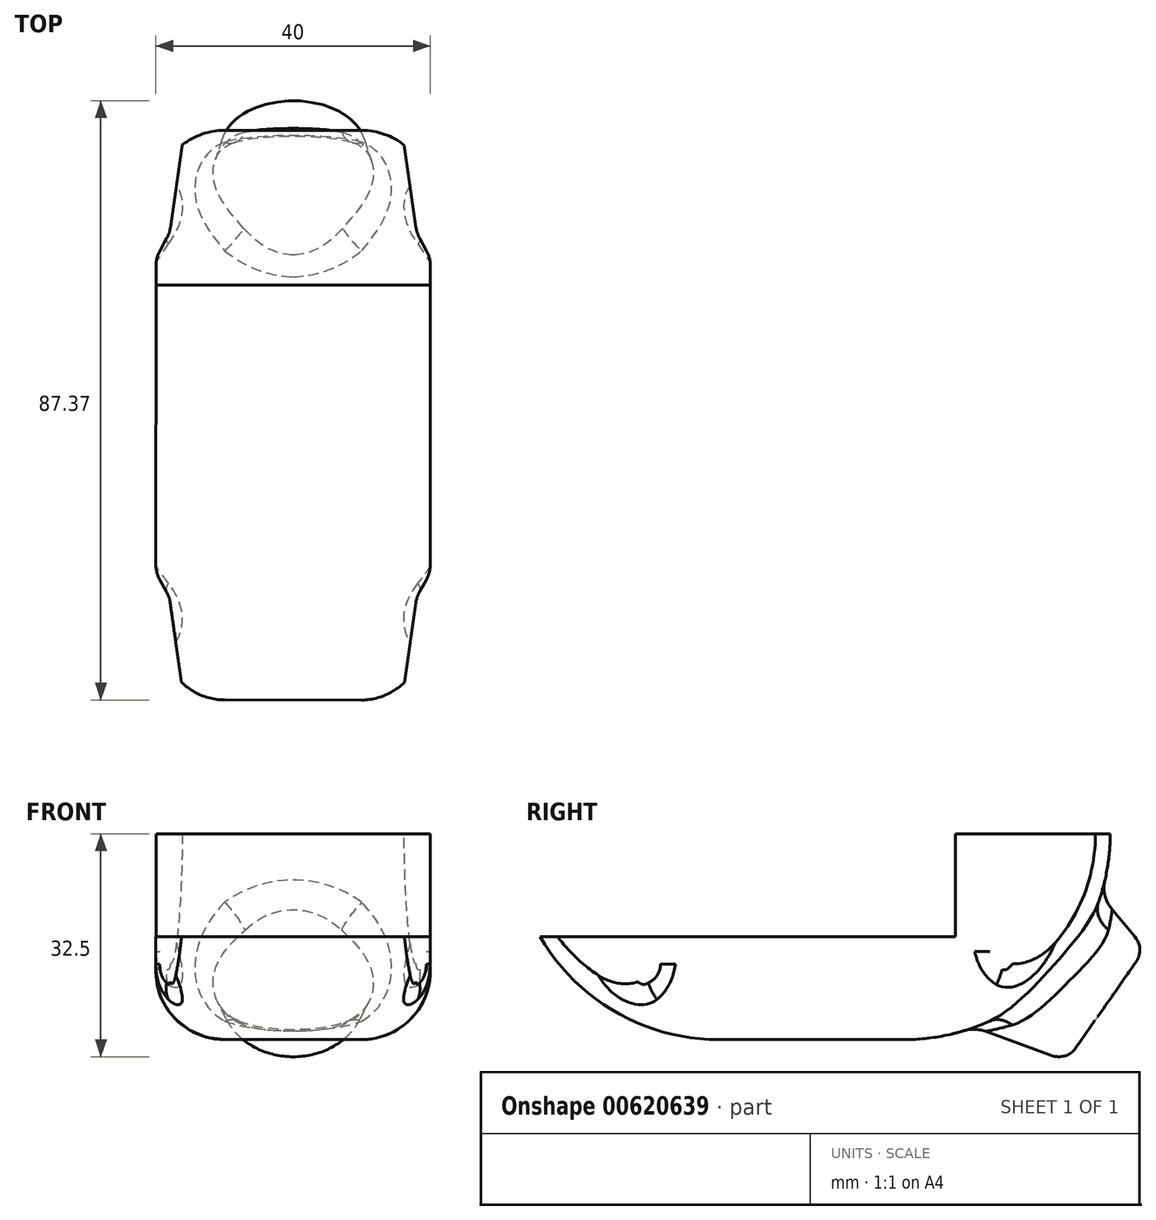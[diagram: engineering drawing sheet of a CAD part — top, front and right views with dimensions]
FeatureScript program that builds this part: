
annotation { "Feature Type Name" : "Feature", "Feature Type Description" : "" }
export const myFeature = defineFeature(function(context is Context, id is Id, definition is map)
    precondition{}
    {
        {
            var Q0;
            Q0=qCreatedBy(makeId("Top.planeOp"),FACE);
            var sketch = newSketch(context, id + "F0", { "sketchPlane" : qUnion([Q0])});
            skLineSegment(sketch, "E0", {"start": v(-20, -22.95) * mm, "end": v(-18.03, -26.5) * mm});
            skLineSegment(sketch, "E1", {"start": v(-18.03, -26.5) * mm, "end": v(-15.88, -41.51) * mm});
            skPoint(sketch, "E2.endSnap0", {"position": v(-0.02, -41.52) * mm});
            skLineSegment(sketch, "E3", {"start": v(-0.02, -41.52) * mm, "end": v(0, 0) * mm, "construction": true});
            skLineSegment(sketch, "E4", {"start": v(-15.88, -41.51) * mm, "end": v(-0.02, -41.52) * mm});
            skLineSegment(sketch, "E5", {"start": v(0, 0) * mm, "end": v(-20, 0.01) * mm, "construction": true});
            skLineSegment(sketch, "E6.MirrorCS", {"start": v(19.98, -22.98) * mm, "end": v(18, -26.52) * mm});
            skLineSegment(sketch, "E7.MirrorCS", {"start": v(18, -26.52) * mm, "end": v(15.84, -41.53) * mm});
            skLineSegment(sketch, "E8.MirrorCS", {"start": v(15.84, -41.53) * mm, "end": v(-0.02, -41.52) * mm});
            skLineSegment(sketch, "E9.MirrorCS", {"start": v(0, 0) * mm, "end": v(20, -0.01) * mm, "construction": true});
            skLineSegment(sketch, "E10", {"start": v(-20, 0.01) * mm, "end": v(-20, -17.03) * mm});
            skLineSegment(sketch, "E11.MirrorCS", {"start": v(20, -0.01) * mm, "end": v(20, -17.05) * mm});
            skLineSegment(sketch, "E12.MirrorCS", {"start": v(18.03, 26.5) * mm, "end": v(15.88, 41.51) * mm});
            skLineSegment(sketch, "E13.MirrorCS", {"start": v(0.02, 41.52) * mm, "end": v(0, 0) * mm, "construction": true});
            skLineSegment(sketch, "E14.MirrorCS", {"start": v(-19.98, 22.98) * mm, "end": v(-18, 26.52) * mm});
            skLineSegment(sketch, "E15.MirrorCS", {"start": v(20, -0.01) * mm, "end": v(20, 17.03) * mm});
            skPoint(sketch, "E16.MirrorP", {"position": v(0.02, 41.52) * mm});
            skLineSegment(sketch, "E17.MirrorCS", {"start": v(-15.84, 41.53) * mm, "end": v(0.02, 41.52) * mm});
            skLineSegment(sketch, "E18.MirrorCS", {"start": v(-18, 26.52) * mm, "end": v(-15.84, 41.53) * mm});
            skLineSegment(sketch, "E19.MirrorCS", {"start": v(-20, 0.01) * mm, "end": v(-20, 17.05) * mm});
            skLineSegment(sketch, "E20.MirrorCS", {"start": v(20, 22.95) * mm, "end": v(18.03, 26.5) * mm});
            skLineSegment(sketch, "E21.MirrorCS", {"start": v(15.88, 41.51) * mm, "end": v(0.02, 41.52) * mm});
            skLineSegment(sketch, "E22", {"start": v(-19.98, 22.98) * mm, "end": v(-20, -22.95) * mm});
            skLineSegment(sketch, "E23", {"start": v(20, 22.95) * mm, "end": v(19.98, -22.98) * mm});
            skSolve(sketch);
        }
        {
            var Q0;
            Q0=makeQuery(id+"F0.imprint","IMPRINT",FACE,{"disambiguationData":[TD([[makeQuery(id+"F0.imprint","IMPRINT",EDGE,{"derivedFrom":sQuery(id+"F0.wireOp",EDGE,"679dddb6-a4d8-4c66-b0c0-365245d2131c.left")}),1.0]])]});
            var Q1;
            Q1=makeQuery(id+"F0.imprint","IMPRINT",FACE,{"disambiguationData":[TD([[makeQuery(id+"F0.imprint","IMPRINT",EDGE,{"derivedFrom":sQuery(id+"F0.wireOp",EDGE,"86fe544a-d19c-4b15-a90d-d04381c5e18d")}),1.0]])]});
            var Q2;
            Q2=makeQuery(id+"F0.imprint","IMPRINT",FACE,{"disambiguationData":[TD([[makeQuery(id+"F0.imprint","IMPRINT",EDGE,{"derivedFrom":sQuery(id+"F0.wireOp",EDGE,"9e7926ad-3512-4c74-b95f-ea411cc99ddc")}),1.0]])]});
            var Q3;
            Q3=makeQuery(id+"F0.imprint","IMPRINT",FACE,{"disambiguationData":[TD([[makeQuery(id+"F0.imprint","IMPRINT",EDGE,{"derivedFrom":sQuery(id+"F0.wireOp",EDGE,"E0")}),1.0]])]});
            extrude(context, id + "F1", {"entities" : qUnion([Q0, Q1, Q2, Q3]), "depth" : 10 * mm, "offsetDistance" : 25 * mm, "hasSecondDirection" : true, "secondDirectionOppositeDirection" : true, "secondDirectionDepth" : 5 * mm});
        }
        {
            var Q0;
            Q0=qCreatedBy(makeId("Top.planeOp"),FACE);
            var sketch = newSketch(context, id + "F2", { "sketchPlane" : qUnion([Q0])});
            skLineSegment(sketch, "E24.MirrorCS", {"start": v(18.03, 26.5) * mm, "end": v(15.88, 41.51) * mm});
            skLineSegment(sketch, "E25.MirrorCS", {"start": v(-19.98, 22.98) * mm, "end": v(-18, 26.52) * mm});
            skPoint(sketch, "E26.MirrorP", {"position": v(0.02, 41.52) * mm});
            skLineSegment(sketch, "E27.MirrorCS", {"start": v(-15.84, 41.53) * mm, "end": v(0.02, 41.52) * mm});
            skLineSegment(sketch, "E28.MirrorCS", {"start": v(-18, 26.52) * mm, "end": v(-15.84, 41.53) * mm});
            skLineSegment(sketch, "E29.MirrorCS", {"start": v(20, 22.95) * mm, "end": v(18.03, 26.5) * mm});
            skLineSegment(sketch, "E30.MirrorCS", {"start": v(15.88, 41.51) * mm, "end": v(0.02, 41.52) * mm});
            skLineSegment(sketch, "E31", {"start": v(-19.98, 19) * mm, "end": v(20, 18.97) * mm});
            skLineSegment(sketch, "E32", {"start": v(-19.98, 22.98) * mm, "end": v(-19.98, 19) * mm});
            skLineSegment(sketch, "E33", {"start": v(20, 22.95) * mm, "end": v(20, 18.97) * mm});
            skSolve(sketch);
        }
        {
            var Q0;
            Q0 = qSketchRegion(id + "F2", true);
            extrude(context, id + "F3", {"entities" : qUnion([Q0]), "operationType" : NewBodyOperationType.ADD, "depth" : 25 * mm, "offsetDistance" : 25 * mm});
        }
        {
            var Q0;
            Q0=makeQuery(id+"F1.opExtrude","CAP_EDGE",EDGE,{"disambiguationData":[OSD([sQuery(id+"F0.wireOp",EDGE,"E17.MirrorCS"),sQuery(id+"F0.wireOp",EDGE,"E21.MirrorCS")])],"isStart":true});
            var Q1;
            Q1=makeQuery(id+"F1.opExtrude","CAP_EDGE",EDGE,{"disambiguationData":[OSD([sQuery(id+"F0.wireOp",EDGE,"E4"),sQuery(id+"F0.wireOp",EDGE,"E8.MirrorCS")])],"isStart":true});
            fillet(context, id + "F4", {"entities" : qUnion([Q0, Q1]), "radius" : 30 * mm, "tangentPropagation" : true, "allowEdgeOverflow" : false});
        }
        {
            var Q0;
            Q0=makeQuery(id+"F1.opExtrude","CAP_EDGE",EDGE,{"disambiguationData":[OSD([sQuery(id+"F0.wireOp",EDGE,"E22")])],"isStart":true});
            var Q1;
            Q1=makeQuery(id+"F1.opExtrude","CAP_EDGE",EDGE,{"disambiguationData":[OSD([sQuery(id+"F0.wireOp",EDGE,"E23")])],"isStart":true});
            fillet(context, id + "F5", {"entities" : qUnion([Q0, Q1]), "radius" : 10 * mm, "tangentPropagation" : true, "allowEdgeOverflow" : false});
        }
        {
            var Q0;
            Q0=makeQuery(id+"F3.boolean.opBoolean","MERGE",EDGE,{"derivedFrom":[makeQuery(id+"F1.opExtrude","SWEPT_EDGE",EDGE,{"disambiguationData":[OSD([sQuery(id+"F0.wireOp",EDGE,"E14.MirrorCS"),sQuery(id+"F0.wireOp",EDGE,"E22")])]}),makeQuery(id+"F3.opExtrude","SWEPT_EDGE",EDGE,{"disambiguationData":[OSD([sQuery(id+"F2.wireOp",EDGE,"E25.MirrorCS"),sQuery(id+"F2.wireOp",EDGE,"E32")])]})]});
            var Q1;
            Q1=makeQuery(id+"F3.boolean.opBoolean","MERGE",EDGE,{"derivedFrom":[makeQuery(id+"F1.opExtrude","SWEPT_EDGE",EDGE,{"disambiguationData":[OSD([sQuery(id+"F0.wireOp",EDGE,"E20.MirrorCS"),sQuery(id+"F0.wireOp",EDGE,"E23")])]}),makeQuery(id+"F3.opExtrude","SWEPT_EDGE",EDGE,{"disambiguationData":[OSD([sQuery(id+"F2.wireOp",EDGE,"E29.MirrorCS"),sQuery(id+"F2.wireOp",EDGE,"E33")])]})]});
            var Q2;
            Q2=makeQuery(id+"F3.boolean.opBoolean","MERGE",EDGE,{"derivedFrom":[makeQuery(id+"F1.opExtrude","SWEPT_EDGE",EDGE,{"disambiguationData":[OSD([sQuery(id+"F0.wireOp",EDGE,"E12.MirrorCS"),sQuery(id+"F0.wireOp",EDGE,"E20.MirrorCS")])]}),makeQuery(id+"F3.opExtrude","SWEPT_EDGE",EDGE,{"disambiguationData":[OSD([sQuery(id+"F2.wireOp",EDGE,"E24.MirrorCS"),sQuery(id+"F2.wireOp",EDGE,"E29.MirrorCS")])]})]});
            var Q3;
            Q3=makeQuery(id+"F3.boolean.opBoolean","MERGE",EDGE,{"derivedFrom":[makeQuery(id+"F1.opExtrude","SWEPT_EDGE",EDGE,{"disambiguationData":[OSD([sQuery(id+"F0.wireOp",EDGE,"E14.MirrorCS"),sQuery(id+"F0.wireOp",EDGE,"E18.MirrorCS")])]}),makeQuery(id+"F3.opExtrude","SWEPT_EDGE",EDGE,{"disambiguationData":[OSD([sQuery(id+"F2.wireOp",EDGE,"E25.MirrorCS"),sQuery(id+"F2.wireOp",EDGE,"E28.MirrorCS")])]})]});
            var Q4;
            Q4=makeQuery(id+"F1.opExtrude","SWEPT_EDGE",EDGE,{"disambiguationData":[OSD([sQuery(id+"F0.wireOp",EDGE,"E0"),sQuery(id+"F0.wireOp",EDGE,"E1")])]});
            var Q5;
            Q5=makeQuery(id+"F1.opExtrude","SWEPT_EDGE",EDGE,{"disambiguationData":[OSD([sQuery(id+"F0.wireOp",EDGE,"E6.MirrorCS"),sQuery(id+"F0.wireOp",EDGE,"E7.MirrorCS")])]});
            var Q6;
            Q6=makeQuery(id+"F1.opExtrude","SWEPT_EDGE",EDGE,{"disambiguationData":[OSD([sQuery(id+"F0.wireOp",EDGE,"E6.MirrorCS"),sQuery(id+"F0.wireOp",EDGE,"E23")])]});
            var Q7;
            Q7=makeQuery(id+"F1.opExtrude","SWEPT_EDGE",EDGE,{"disambiguationData":[OSD([sQuery(id+"F0.wireOp",EDGE,"E0"),sQuery(id+"F0.wireOp",EDGE,"E22")])]});
            fillet(context, id + "F6", {"entities" : qUnion([Q0, Q1, Q2, Q3, Q4, Q5, Q6, Q7]), "radius" : 4.5 * mm, "tangentPropagation" : true, "allowEdgeOverflow" : false});
        }
        {
            var Q0;
            Q0=makeQuery(id+"F4.opFillet","BLEND_EDGE",EDGE,{"blendedFrom":[makeQuery(id+"F1.opExtrude","CAP_EDGE",EDGE,{"disambiguationData":[OSD([sQuery(id+"F0.wireOp",EDGE,"E17.MirrorCS"),sQuery(id+"F0.wireOp",EDGE,"E21.MirrorCS")])],"isStart":true}),makeQuery(id+"F3.opExtrude","CAP_FACE",FACE,{"disambiguationData":[OSD([sQuery(id+"F2.wireOp",EDGE,"E24.MirrorCS"),sQuery(id+"F2.wireOp",EDGE,"E25.MirrorCS"),sQuery(id+"F2.wireOp",EDGE,"E27.MirrorCS"),sQuery(id+"F2.wireOp",EDGE,"E28.MirrorCS"),sQuery(id+"F2.wireOp",EDGE,"E29.MirrorCS"),sQuery(id+"F2.wireOp",EDGE,"E30.MirrorCS"),sQuery(id+"F2.wireOp",EDGE,"E31"),sQuery(id+"F2.wireOp",EDGE,"E32"),sQuery(id+"F2.wireOp",EDGE,"E33")])],"isStart":false})],"blendedInto":[makeQuery(id+"F3.opExtrude","CAP_FACE",FACE,{"disambiguationData":[OSD([sQuery(id+"F2.wireOp",EDGE,"E24.MirrorCS"),sQuery(id+"F2.wireOp",EDGE,"E25.MirrorCS"),sQuery(id+"F2.wireOp",EDGE,"E27.MirrorCS"),sQuery(id+"F2.wireOp",EDGE,"E28.MirrorCS"),sQuery(id+"F2.wireOp",EDGE,"E29.MirrorCS"),sQuery(id+"F2.wireOp",EDGE,"E30.MirrorCS"),sQuery(id+"F2.wireOp",EDGE,"E31"),sQuery(id+"F2.wireOp",EDGE,"E32"),sQuery(id+"F2.wireOp",EDGE,"E33")])],"isStart":false})]});
            cPlane(context, id + "F7", {"entities" : qUnion([Q0]), "cplaneType" : CPlaneType.LINE_ANGLE, "offset" : 25 * mm, "angle" : 35 * degree, "width" : 150 * mm, "height" : 150 * mm});
        }
        {
            var Q0;
            Q0=qCreatedBy(id+"F7.planeOp",FACE);
            var sketch = newSketch(context, id + "F8", { "sketchPlane" : qUnion([Q0])});
            skCircle(sketch, "E34", {"center": v(0, 23.5) * mm, "radius": 14.79 * mm});
            skSolve(sketch);
        }
        {
            var Q0;
            Q0 = qSketchRegion(id + "F8", true);
            extrude(context, id + "F9", {"entities" : qUnion([Q0]), "operationType" : NewBodyOperationType.ADD, "oppositeDirection" : true, "depth" : 13.8 * mm, "offsetDistance" : 25 * mm});
        }
        {
            var Q0;
            Q0=makeQuery(id+"F9.opExtrude","CAP_FACE",FACE,{"disambiguationData":[OSD([sQuery(id+"F8.wireOp",EDGE,"E34")])],"isStart":false});
            chamfer(context, id + "F10", {"entities" : qUnion([Q0]), "chamferType" : ChamferType.OFFSET_ANGLE, "width" : 18 * mm, "oppositeDirection" : false, "angle" : 15 * degree, "tangentPropagation" : true});
        }
        {
            var Q0;
            {var subQ0=sQuery(id+"F8.wireOp",EDGE,"E34");Q0=makeQuery(id+"F10.opChamfer","BLEND_EDGE",EDGE,{"blendedFrom":[makeQuery(id+"F9.opExtrude","CAP_EDGE",EDGE,{"disambiguationData":[OSD([subQ0])],"isStart":false}),makeQuery(id+"F9.opExtrude","CAP_FACE",FACE,{"disambiguationData":[OSD([subQ0])],"isStart":false})],"blendedInto":[makeQuery(id+"F9.opExtrude","CAP_FACE",FACE,{"disambiguationData":[OSD([subQ0])],"isStart":false})]});}
            fillet(context, id + "F11", {"entities" : qUnion([Q0]), "radius" : 3 * mm, "tangentPropagation" : true, "allowEdgeOverflow" : false});
        }
        {
            var Q0;
            {var subQ0=sQuery(id+"F8.wireOp",EDGE,"E34");Q0=makeQuery(id+"F10.opChamfer","BLEND_EDGE",EDGE,{"blendedFrom":[makeQuery(id+"F9.opExtrude","CAP_EDGE",EDGE,{"disambiguationData":[OSD([subQ0])],"isStart":false}),makeQuery(id+"F9.opExtrude","CAP_FACE",FACE,{"disambiguationData":[OSD([subQ0])],"isStart":true})],"blendedInto":[makeQuery(id+"F9.opExtrude","CAP_FACE",FACE,{"disambiguationData":[OSD([subQ0])],"isStart":true})]});}
            var Q1;
            {var subQ0=sQuery(id+"F0.wireOp",EDGE,"E22");var subQ2=sQuery(id+"F0.wireOp",EDGE,"E21.MirrorCS");var subQ3=sQuery(id+"F0.wireOp",EDGE,"E17.MirrorCS");var subQ4=sQuery(id+"F8.wireOp",EDGE,"E34");Q1=makeQuery(id+"F10.opChamfer","BLEND_EDGE",EDGE,{"disambiguationData":[OD(1.0)],"blendedFrom":[makeQuery(id+"F9.opExtrude","CAP_EDGE",EDGE,{"disambiguationData":[OSD([subQ4])],"isStart":false}),makeQuery(id+"F9.boolean.opBoolean","SPLIT",FACE,{"disambiguationData":[TD([makeQuery(id+"F5.opFillet","BLEND_FACE",FACE,{"disambiguationData":[OSD([subQ0])]})])],"derivedFrom":makeQuery(id+"F4.opFillet","BLEND_FACE",FACE,{"disambiguationData":[OSD([subQ3,subQ2])]})})],"blendedInto":[makeQuery(id+"F9.boolean.opBoolean","SPLIT",FACE,{"disambiguationData":[TD([makeQuery(id+"F5.opFillet","BLEND_FACE",FACE,{"disambiguationData":[OSD([subQ0])]})])],"derivedFrom":makeQuery(id+"F4.opFillet","BLEND_FACE",FACE,{"disambiguationData":[OSD([subQ3,subQ2])]})})]});}
            var Q2;
            Q2=makeQuery(id+"F10.opChamfer","BLEND_FACE",FACE,{"disambiguationData":[OSD([sQuery(id+"F8.wireOp",EDGE,"E34")])]});
            fillet(context, id + "F12", {"entities" : qUnion([Q0, Q1, Q2]), "radius" : 5 * mm, "tangentPropagation" : true, "allowEdgeOverflow" : false});
        }
    });
